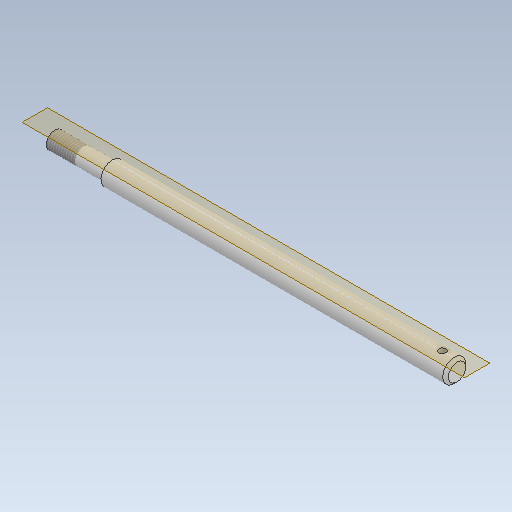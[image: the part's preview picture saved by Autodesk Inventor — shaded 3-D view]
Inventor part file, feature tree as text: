
AUTODESK INVENTOR PART (.ipt)
format: ipt  version: 2021 (Build 250183000, 183)  size: 118,272 bytes
history: native  units: mm
features: sketch x2, revolve x1, thread x1, plane x1, extrude x1
ambient origin geometry x8: Origin, YZ Plane, XZ Plane, XY Plane, X Axis, Y Axis, Z Axis, Center Point
bodies: Solid1 (feature_tree)
feature tree (6):
  revolve  "Revolution1"  [1 undecoded]
  thread  "Thread1"  [1 undecoded]
  plane  "Work Plane1"
  extrude  "Extrusion1"  Depth=10.0mm
  sketch  "Sketch1"  dims[d0=280.0mm d1=8.0mm d2=6.0mm]
  sketch  "Sketch2"  dims[d3=40.0mm d4=2.0mm d5=2.0mm d6=45.0deg d7=90.0deg d9=20.0mm d10=0.0mm d11=8.0mm d12=5.0mm d13=10.0mm d14=270.0mm d15=0.0mm d16=0.0mm]
note: 2 required parameter values undecoded (feature->parameter linkage not recoverable at this tier; creation-order binding heuristic only, values carry confidence <= 0.55)